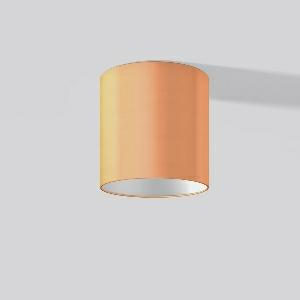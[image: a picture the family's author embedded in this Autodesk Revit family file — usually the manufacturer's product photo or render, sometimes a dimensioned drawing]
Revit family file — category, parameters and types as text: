
# Revit family: toledo_flatliner_901634_002_1_76_f2e0
name_source: partatom
category: Lighting Fixtures
units: mm (PartAtom-declared; Revit-internal decimal feet)

## family parameters
Cut with Voids When Loaded = No
Host = Face
Light Source = No
Part Type = Normal
Room Calculation Point = No
Round Connector Dimension = Use Diameter
Shared = No

## types (1)
- 982302.002 (1 x LED Modul 840, 1950 lm, 4000)
    Apparent Load = 22 VA
    CIE Flux Codes = 50 82 97 99 100
    Color Rendering = 80
    Color Temperature = 4000
    Default Elevation = 1800 mm
    Description = Series: TOLEDO FLATLINER
Decorative ceiling luminaire for interior decoration. Base luminaire prepared for the installation of fabric lampshade. Cylinder housing sheet steel, powder-coated. Housing: die cast aluminium and sheet steel, powder-coated. Bezel ring: die-cast aluminium, powder-coated. Lightguide and diffuser made of non-yellowing plastic (PMMA) opal matt. Modular design: With the basic luminaire, a square or cylindrical fabric lampshade must always be ordered separately. Fabric lampshades can be fitted to the basic luminaire without tools. Order satin finish diffuser as separate accessory. 
Colour: white
Diameter: 330 mm
Height: 70 mm
Lamp: LED
Socket: without socket
Colour temperature: 4000K
Colour rendering index (CRI): 80
System power: 22 W
Rated luminous flux: 1950 lm
Luminous efficiency: 89 lm/W
Control gear: Converter, dimmable, DALI
Protection class: II
Type of protection: IP 40
    Height = 70 mm
    Lamp = 1 x LED Modul 840
    Lamp Light Flux = 1950 lm
    Lamp count = 1
    Length = 330 mm
    Lifetime = 50000 h
    Luminous efficacy = 89 lm/W
    Manufacturer = RZB
    ModVariant = No
    Model = 901634.002.1.76
    Mounting Place = Ceiling
    Mounting Type = Surface mounted
    Number of Poles = 1
    OnlyDefault = Yes
    Power Factor = 1
    Product Name = TOLEDO FLATLINER
    Product group = Surface mounted ceiling Fabric lampshade luminaires
    ProductGroupID = 313
    Protection Class = Protection class II
    Protection Degree = IP 40
    RLX_Detail_Level = 1
    RLX_Emergency_Light_Flux = 0 lm
    RLX_Emergency_Type = 0
    RLX_Emergency_Type_DB = No
    RlxData = <blob elided: 62769 chars, md5=d8010010>
    Socket = socket
    Standby Power = 0 W
    System Light Flux = 1950 lm
    System Power = 22 W
    Type Image = toledo_flatliner_anbau_rund_orange_odeckel.jpg
    URL = http://relux.com
    VarID = 982302_002_891e
    Voltage = 230 V
    Voltage Range = 220-240 V
    Weight = 0.00 kg
    Width = 0 mm  [stored 0 ft]

note: [stored X ft] marks values corroborated as IEEE doubles in the binary element streams (Revit-internal decimal feet)

## geometry (parser evidence)
native form markers: Blend x4, Sweep x10
no freeform markers — native parametric forms only
